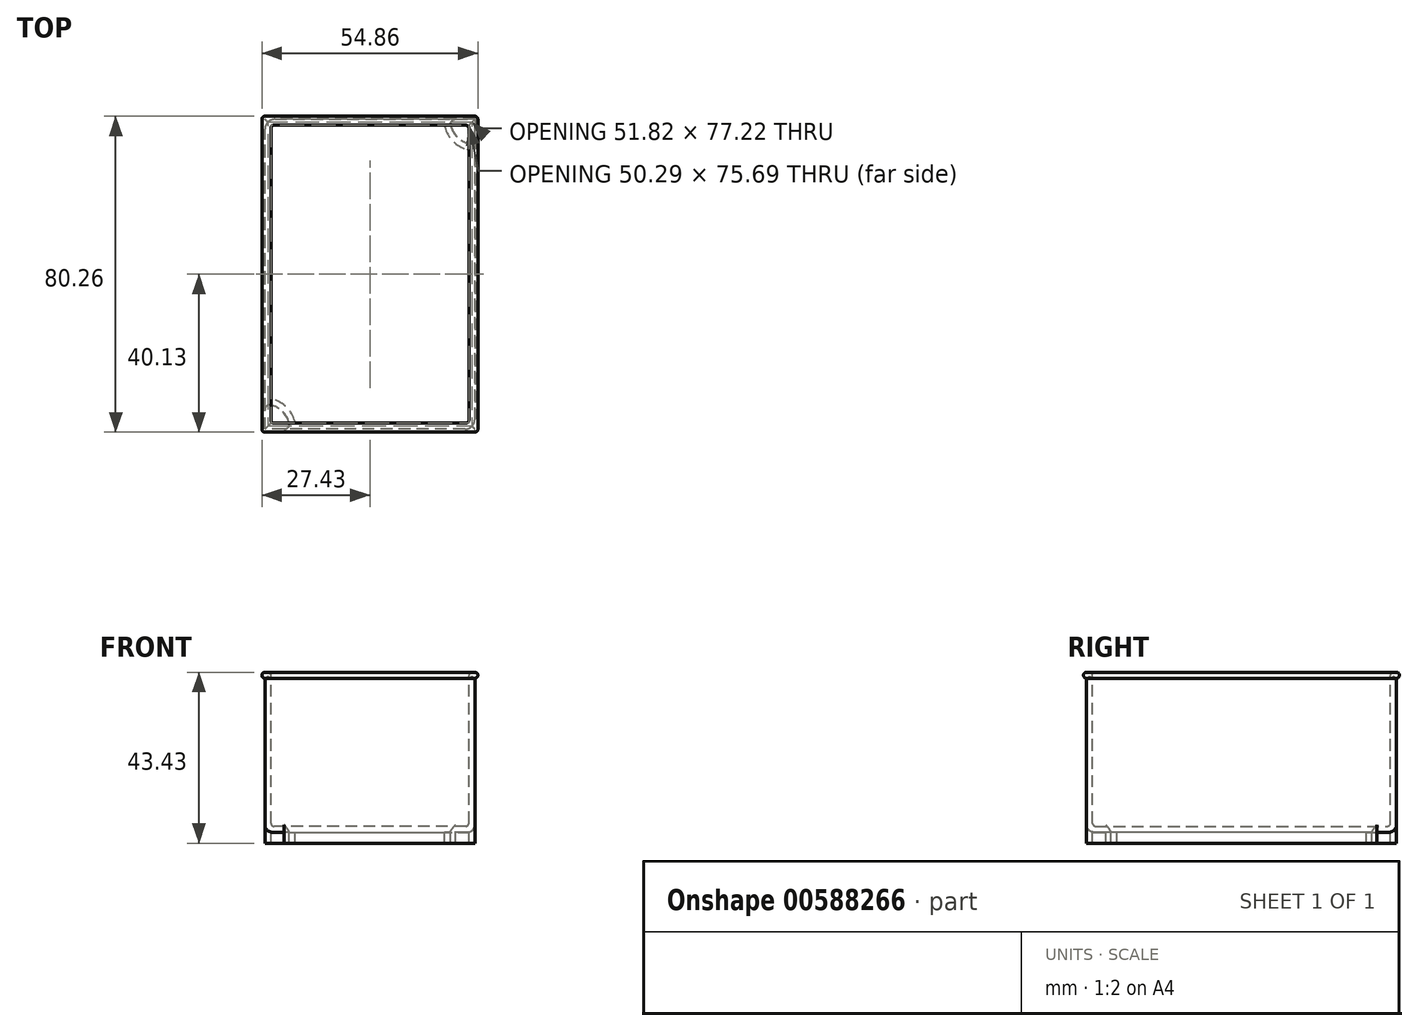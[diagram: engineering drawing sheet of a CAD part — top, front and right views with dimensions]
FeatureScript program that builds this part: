
annotation { "Feature Type Name" : "Feature", "Feature Type Description" : "" }
export const myFeature = defineFeature(function(context is Context, id is Id, definition is map)
    precondition{}
    {
        {
            var Q0;
            Q0=qCreatedBy(makeId("Front.planeOp"),FACE);
            var sketch = newSketch(context, id + "F0", { "sketchPlane" : qUnion([Q0])});
            skLineSegment(sketch, "E0.bottom", {"start": v(26.67, -20.32) * mm, "end": v(-26.67, -20.32) * mm});
            skLineSegment(sketch, "E0.top", {"start": v(26.67, 20.32) * mm, "end": v(-26.67, 20.32) * mm});
            skLineSegment(sketch, "E0.left", {"start": v(26.67, -20.32) * mm, "end": v(26.67, 20.32) * mm});
            skLineSegment(sketch, "E0.right", {"start": v(-26.67, -20.32) * mm, "end": v(-26.67, 20.32) * mm});
            skPoint(sketch, "E0.middle", {"position": v(0, 0) * mm});
            skSolve(sketch);
        }
        {
            var Q0;
            Q0=makeQuery(id+"F0.imprint","IMPRINT",FACE,{"disambiguationData":[TD([[makeQuery(id+"F0.imprint","IMPRINT",EDGE,{"derivedFrom":sQuery(id+"F0.wireOp",EDGE,"E0.bottom")}),-1.0]])]});
            extrude(context, id + "F1", {"entities" : qUnion([Q0]), "endBound" : BoundingType.SYMMETRIC, "depth" : 78.74 * mm});
        }
        {
            var Q0;
            Q0=makeQuery(id+"F1.opExtrude","SWEPT_FACE",FACE,{"disambiguationData":[OSD([sQuery(id+"F0.wireOp",EDGE,"E0.top")])]});
            shell(context, id + "F2", {"entities" : qUnion([Q0]), "thickness" : 1.52 * mm});
        }
        {
            var Q0;
            Q0=makeQuery(id+"F1.opExtrude","CAP_FACE",FACE,{"disambiguationData":[OSD([sQuery(id+"F0.wireOp",EDGE,"E0.bottom"),sQuery(id+"F0.wireOp",EDGE,"E0.top"),sQuery(id+"F0.wireOp",EDGE,"E0.left"),sQuery(id+"F0.wireOp",EDGE,"E0.right")])],"isStart":false});
            var sketch = newSketch(context, id + "F3", { "sketchPlane" : qUnion([Q0])});
            skArc(sketch, "E1", {"start": v(-26.67, 20.32) * mm, "mid": v(-27.43, 19.56) * mm, "end": v(-26.67, 18.8) * mm});
            skSolve(sketch);
        }
        {
            var Q0;
            {var subQ0=sQuery(id+"F3.wireOp",EDGE,"E1");Q0=makeQuery(id+"F3.imprint","IMPRINT",FACE,{"disambiguationData":[TD([[makeQuery(id+"F3.imprint","IMPRINT",EDGE,{"derivedFrom":subQ0}),1.0]])]});}
            var Q1;
            Q1=makeQuery(id+"F1.opExtrude","SWEPT_EDGE",EDGE,{"disambiguationData":[OSD([sQuery(id+"F0.wireOp",EDGE,"E0.top"),sQuery(id+"F0.wireOp",EDGE,"E0.right")])]});
            var Q2;
            Q2=makeQuery(id+"F1.opExtrude","CAP_EDGE",EDGE,{"disambiguationData":[OSD([sQuery(id+"F0.wireOp",EDGE,"E0.top")])],"isStart":true});
            var Q3;
            Q3=makeQuery(id+"F1.opExtrude","SWEPT_EDGE",EDGE,{"disambiguationData":[OSD([sQuery(id+"F0.wireOp",EDGE,"E0.top"),sQuery(id+"F0.wireOp",EDGE,"E0.left")])]});
            var Q4;
            Q4=makeQuery(id+"F1.opExtrude","CAP_EDGE",EDGE,{"disambiguationData":[OSD([sQuery(id+"F0.wireOp",EDGE,"E0.top")])],"isStart":false});
            sweep(context, id + "F4", {"operationType" : NewBodyOperationType.ADD, "profiles" : qUnion([Q0]), "path" : qUnion([Q1, Q2, Q3, Q4])});
        }
        {
            var Q0;
            Q0=makeQuery(id+"F1.opExtrude","SWEPT_FACE",FACE,{"disambiguationData":[OSD([sQuery(id+"F0.wireOp",EDGE,"E0.bottom")])]});
            var sketch = newSketch(context, id + "F5", { "sketchPlane" : qUnion([Q0])});
            skLineSegment(sketch, "E2.bottom", {"start": v(26.67, 39.37) * mm, "end": v(21.75, 39.37) * mm});
            skLineSegment(sketch, "E2.left", {"start": v(26.67, 39.37) * mm, "end": v(26.67, 34.45) * mm});
            skPoint(sketch, "E3.newPointA", {"position": v(20.32, 19.05) * mm});
            skArc(sketch, "E4", {"start": v(20.52, 37.78) * mm, "mid": v(22.18, 34.88) * mm, "end": v(25.08, 33.22) * mm});
            skPoint(sketch, "E5.visualSharp", {"position": v(20.32, 39.37) * mm});
            skArc(sketch, "E5.filletArc", {"start": v(21.75, 39.37) * mm, "mid": v(20.75, 38.88) * mm, "end": v(20.52, 37.78) * mm});
            skPoint(sketch, "E6.visualSharp", {"position": v(26.67, 33.02) * mm});
            skArc(sketch, "E6.filletArc", {"start": v(25.08, 33.22) * mm, "mid": v(26.18, 33.45) * mm, "end": v(26.67, 34.45) * mm});
            skArc(sketch, "E7.MirrorCS", {"start": v(-21.75, 39.37) * mm, "mid": v(-20.75, 38.88) * mm, "end": v(-20.52, 37.78) * mm});
            skArc(sketch, "E8.MirrorCS", {"start": v(-20.52, 37.78) * mm, "mid": v(-22.18, 34.88) * mm, "end": v(-25.08, 33.22) * mm});
            skArc(sketch, "E9.MirrorCS", {"start": v(-25.08, 33.22) * mm, "mid": v(-26.18, 33.45) * mm, "end": v(-26.67, 34.45) * mm});
            skLineSegment(sketch, "E10.MirrorCS", {"start": v(-26.67, 39.37) * mm, "end": v(-26.67, 34.45) * mm});
            skLineSegment(sketch, "E11.MirrorCS", {"start": v(-26.67, 39.37) * mm, "end": v(-21.75, 39.37) * mm});
            skArc(sketch, "E12.MirrorCS", {"start": v(-20.52, -37.78) * mm, "mid": v(-22.18, -34.88) * mm, "end": v(-25.08, -33.22) * mm});
            skArc(sketch, "E13.MirrorCS", {"start": v(-21.75, -39.37) * mm, "mid": v(-20.75, -38.88) * mm, "end": v(-20.52, -37.78) * mm});
            skLineSegment(sketch, "E14.MirrorCS", {"start": v(-26.67, -39.37) * mm, "end": v(-21.75, -39.37) * mm});
            skLineSegment(sketch, "E15.MirrorCS", {"start": v(-26.67, -39.37) * mm, "end": v(-26.67, -34.45) * mm});
            skArc(sketch, "E16.MirrorCS", {"start": v(-25.08, -33.22) * mm, "mid": v(-26.18, -33.45) * mm, "end": v(-26.67, -34.45) * mm});
            skArc(sketch, "E17.MirrorCS", {"start": v(21.75, -39.37) * mm, "mid": v(20.75, -38.88) * mm, "end": v(20.52, -37.78) * mm});
            skArc(sketch, "E18.MirrorCS", {"start": v(20.52, -37.78) * mm, "mid": v(22.18, -34.88) * mm, "end": v(25.08, -33.22) * mm});
            skArc(sketch, "E19.MirrorCS", {"start": v(25.08, -33.22) * mm, "mid": v(26.18, -33.45) * mm, "end": v(26.67, -34.45) * mm});
            skLineSegment(sketch, "E20.MirrorCS", {"start": v(26.67, -39.37) * mm, "end": v(26.67, -34.45) * mm});
            skLineSegment(sketch, "E21.MirrorCS", {"start": v(26.67, -39.37) * mm, "end": v(21.75, -39.37) * mm});
            skSolve(sketch);
        }
        {
            var Q0;
            Q0=makeQuery(id+"F5.imprint","IMPRINT",FACE,{"disambiguationData":[TD([[makeQuery(id+"F5.imprint","IMPRINT",EDGE,{"derivedFrom":sQuery(id+"F5.wireOp",EDGE,"E2.bottom")}),1.0]])]});
            var Q1;
            Q1=makeQuery(id+"F5.imprint","IMPRINT",FACE,{"disambiguationData":[TD([[makeQuery(id+"F5.imprint","IMPRINT",EDGE,{"derivedFrom":sQuery(id+"F5.wireOp",EDGE,"E8.MirrorCS")}),-1.0]])]});
            var Q2;
            Q2=makeQuery(id+"F5.imprint","IMPRINT",FACE,{"disambiguationData":[TD([[makeQuery(id+"F5.imprint","IMPRINT",EDGE,{"derivedFrom":sQuery(id+"F5.wireOp",EDGE,"E12.MirrorCS")}),1.0]])]});
            var Q3;
            Q3=makeQuery(id+"F5.imprint","IMPRINT",FACE,{"disambiguationData":[TD([[makeQuery(id+"F5.imprint","IMPRINT",EDGE,{"derivedFrom":sQuery(id+"F5.wireOp",EDGE,"E17.MirrorCS")}),-1.0]])]});
            extrude(context, id + "F6", {"entities" : qUnion([Q0, Q1, Q2, Q3]), "operationType" : NewBodyOperationType.ADD, "depth" : 2.8 * mm});
        }
        {
            var Q0;
            Q0=makeQuery(id+"F6.opExtrude","CAP_FACE",FACE,{"disambiguationData":[OSD([sQuery(id+"F5.wireOp",EDGE,"E2.bottom"),sQuery(id+"F5.wireOp",EDGE,"E2.left"),sQuery(id+"F5.wireOp",EDGE,"E4"),sQuery(id+"F5.wireOp",EDGE,"E5.filletArc"),sQuery(id+"F5.wireOp",EDGE,"E6.filletArc")])],"isStart":false});
            var Q1;
            Q1=makeQuery(id+"F6.opExtrude","CAP_FACE",FACE,{"disambiguationData":[OSD([sQuery(id+"F5.wireOp",EDGE,"E8.MirrorCS"),sQuery(id+"F5.wireOp",EDGE,"E9.MirrorCS"),sQuery(id+"F5.wireOp",EDGE,"E10.MirrorCS"),sQuery(id+"F5.wireOp",EDGE,"E7.MirrorCS"),sQuery(id+"F5.wireOp",EDGE,"E11.MirrorCS")])],"isStart":false});
            var Q2;
            Q2=makeQuery(id+"F6.opExtrude","CAP_FACE",FACE,{"disambiguationData":[OSD([sQuery(id+"F5.wireOp",EDGE,"E12.MirrorCS"),sQuery(id+"F5.wireOp",EDGE,"E13.MirrorCS"),sQuery(id+"F5.wireOp",EDGE,"E14.MirrorCS"),sQuery(id+"F5.wireOp",EDGE,"E15.MirrorCS"),sQuery(id+"F5.wireOp",EDGE,"E16.MirrorCS")])],"isStart":false});
            var Q3;
            Q3=makeQuery(id+"F6.opExtrude","CAP_FACE",FACE,{"disambiguationData":[OSD([sQuery(id+"F5.wireOp",EDGE,"E17.MirrorCS"),sQuery(id+"F5.wireOp",EDGE,"E18.MirrorCS"),sQuery(id+"F5.wireOp",EDGE,"E19.MirrorCS"),sQuery(id+"F5.wireOp",EDGE,"E20.MirrorCS"),sQuery(id+"F5.wireOp",EDGE,"E21.MirrorCS")])],"isStart":false});
            shell(context, id + "F7", {"entities" : qUnion([Q0, Q1, Q2, Q3]), "thickness" : 1.52 * mm});
        }
        {
            var Q0;
            Q0=makeQuery(id+"F2.opShell","OFFSET_FACE",FACE,{"disambiguationData":[OSD([sQuery(id+"F0.wireOp",EDGE,"E0.left")])]});
            var Q1;
            {var subQ0=sQuery(id+"F0.wireOp",EDGE,"E0.right");var subQ1=sQuery(id+"F0.wireOp",EDGE,"E0.left");var subQ2=sQuery(id+"F0.wireOp",EDGE,"E0.top");var subQ3=sQuery(id+"F0.wireOp",EDGE,"E0.bottom");Q1=makeQuery(id+"F2.opShell","OFFSET_FACE",FACE,{"disambiguationData":[OSD([subQ3,subQ2,subQ1,subQ0]),TDD([makeQuery(id+"F1.opExtrude","CAP_FACE",FACE,{"disambiguationData":[OSD([subQ3,subQ2,subQ1,subQ0])],"isStart":true})])]});}
            var Q2;
            Q2=makeQuery(id+"F2.opShell","OFFSET_FACE",FACE,{"disambiguationData":[OSD([sQuery(id+"F0.wireOp",EDGE,"E0.right")])]});
            var Q3;
            {var subQ0=sQuery(id+"F0.wireOp",EDGE,"E0.right");var subQ1=sQuery(id+"F0.wireOp",EDGE,"E0.left");var subQ2=sQuery(id+"F0.wireOp",EDGE,"E0.top");var subQ3=sQuery(id+"F0.wireOp",EDGE,"E0.bottom");Q3=makeQuery(id+"F2.opShell","OFFSET_FACE",FACE,{"disambiguationData":[OSD([subQ3,subQ2,subQ1,subQ0]),TDD([makeQuery(id+"F1.opExtrude","CAP_FACE",FACE,{"disambiguationData":[OSD([subQ3,subQ2,subQ1,subQ0])],"isStart":false})])]});}
            fillet(context, id + "F8", {"entities" : qUnion([Q0, Q1, Q2, Q3]), "radius" : 0.76 * mm, "tangentPropagation" : true, "allowEdgeOverflow" : false});
        }
        {
            var Q0;
            Q0=makeQuery(id+"F1.opExtrude","SWEPT_EDGE",EDGE,{"disambiguationData":[OSD([sQuery(id+"F0.wireOp",EDGE,"E0.bottom"),sQuery(id+"F0.wireOp",EDGE,"E0.right")])]});
            var Q1;
            Q1=makeQuery(id+"F1.opExtrude","CAP_EDGE",EDGE,{"disambiguationData":[OSD([sQuery(id+"F0.wireOp",EDGE,"E0.bottom")])],"isStart":false});
            var Q2;
            Q2=makeQuery(id+"F1.opExtrude","SWEPT_EDGE",EDGE,{"disambiguationData":[OSD([sQuery(id+"F0.wireOp",EDGE,"E0.bottom"),sQuery(id+"F0.wireOp",EDGE,"E0.left")])]});
            var Q3;
            Q3=makeQuery(id+"F1.opExtrude","CAP_EDGE",EDGE,{"disambiguationData":[OSD([sQuery(id+"F0.wireOp",EDGE,"E0.bottom")])],"isStart":true});
            fillet(context, id + "F9", {"entities" : qUnion([Q0, Q1, Q2, Q3]), "radius" : 1.9 * mm, "tangentPropagation" : true, "allowEdgeOverflow" : false});
        }
        {
            var Q0;
            Q0=makeQuery(id+"F4.opSweep","MID_CAP_EDGE",EDGE,{"disambiguationData":[OSD([sQuery(id+"F0.wireOp",EDGE,"E0.top"),sQuery(id+"F0.wireOp",EDGE,"E0.left"),sQuery(id+"F3.wireOp",EDGE,"E1")])],"capPos":3.0});
            var Q1;
            Q1=makeQuery(id+"F4.opSweep","MID_CAP_EDGE",EDGE,{"disambiguationData":[OSD([sQuery(id+"F0.wireOp",EDGE,"E0.top"),sQuery(id+"F0.wireOp",EDGE,"E0.left"),sQuery(id+"F3.wireOp",EDGE,"E1")])],"capPos":2.0});
            var Q2;
            Q2=makeQuery(id+"F4.opSweep","MID_CAP_EDGE",EDGE,{"disambiguationData":[OSD([sQuery(id+"F0.wireOp",EDGE,"E0.top"),sQuery(id+"F0.wireOp",EDGE,"E0.right"),sQuery(id+"F3.wireOp",EDGE,"E1")])],"capPos":1.0});
            var Q3;
            Q3=makeQuery(id+"F4.opSweep","CAP_EDGE",EDGE,{"disambiguationData":[OSD([sQuery(id+"F0.wireOp",EDGE,"E0.top"),sQuery(id+"F0.wireOp",EDGE,"E0.right"),sQuery(id+"F3.wireOp",EDGE,"E1")])],"isStart":true});
            fillet(context, id + "F10", {"entities" : qUnion([Q0, Q1, Q2, Q3]), "radius" : 0.76 * mm, "tangentPropagation" : true, "allowEdgeOverflow" : false});
        }
        {
            var Q0;
            Q0=makeQuery(id+"F6.boolean.opBoolean","MERGE",EDGE,{"derivedFrom":[makeQuery(id+"F1.opExtrude","CAP_EDGE",EDGE,{"disambiguationData":[OSD([sQuery(id+"F0.wireOp",EDGE,"E0.left")])],"isStart":false}),makeQuery(id+"F6.opExtrude","SWEPT_EDGE",EDGE,{"disambiguationData":[OSD([sQuery(id+"F5.wireOp",EDGE,"E2.bottom"),sQuery(id+"F5.wireOp",EDGE,"E2.left")])]})]});
            var Q1;
            Q1=makeQuery(id+"F6.boolean.opBoolean","MERGE",EDGE,{"derivedFrom":[makeQuery(id+"F1.opExtrude","CAP_EDGE",EDGE,{"disambiguationData":[OSD([sQuery(id+"F0.wireOp",EDGE,"E0.left")])],"isStart":true}),makeQuery(id+"F6.opExtrude","SWEPT_EDGE",EDGE,{"disambiguationData":[OSD([sQuery(id+"F5.wireOp",EDGE,"E20.MirrorCS"),sQuery(id+"F5.wireOp",EDGE,"E21.MirrorCS")])]})]});
            var Q2;
            Q2=makeQuery(id+"F6.boolean.opBoolean","MERGE",EDGE,{"derivedFrom":[makeQuery(id+"F1.opExtrude","CAP_EDGE",EDGE,{"disambiguationData":[OSD([sQuery(id+"F0.wireOp",EDGE,"E0.right")])],"isStart":false}),makeQuery(id+"F6.opExtrude","SWEPT_EDGE",EDGE,{"disambiguationData":[OSD([sQuery(id+"F5.wireOp",EDGE,"E10.MirrorCS"),sQuery(id+"F5.wireOp",EDGE,"E11.MirrorCS")])]})]});
            var Q3;
            Q3=makeQuery(id+"F6.boolean.opBoolean","MERGE",EDGE,{"derivedFrom":[makeQuery(id+"F1.opExtrude","CAP_EDGE",EDGE,{"disambiguationData":[OSD([sQuery(id+"F0.wireOp",EDGE,"E0.right")])],"isStart":true}),makeQuery(id+"F6.opExtrude","SWEPT_EDGE",EDGE,{"disambiguationData":[OSD([sQuery(id+"F5.wireOp",EDGE,"E14.MirrorCS"),sQuery(id+"F5.wireOp",EDGE,"E15.MirrorCS")])]})]});
            fillet(context, id + "F11", {"entities" : qUnion([Q0, Q1, Q2, Q3]), "radius" : 2.54 * mm, "tangentPropagation" : true, "allowEdgeOverflow" : false});
        }
        {
            var Q0;
            Q0=makeQuery(id+"F1.opExtrude","SWEPT_BODY",BODY,{"disambiguationData":[OSD([sQuery(id+"F0.wireOp",EDGE,"E0.bottom"),sQuery(id+"F0.wireOp",EDGE,"E0.top"),sQuery(id+"F0.wireOp",EDGE,"E0.left"),sQuery(id+"F0.wireOp",EDGE,"E0.right")])]});
            transform(context, id + "F12", {"entities" : qUnion([Q0]), "transformType" : TransformType.COPY});
        }
    });
